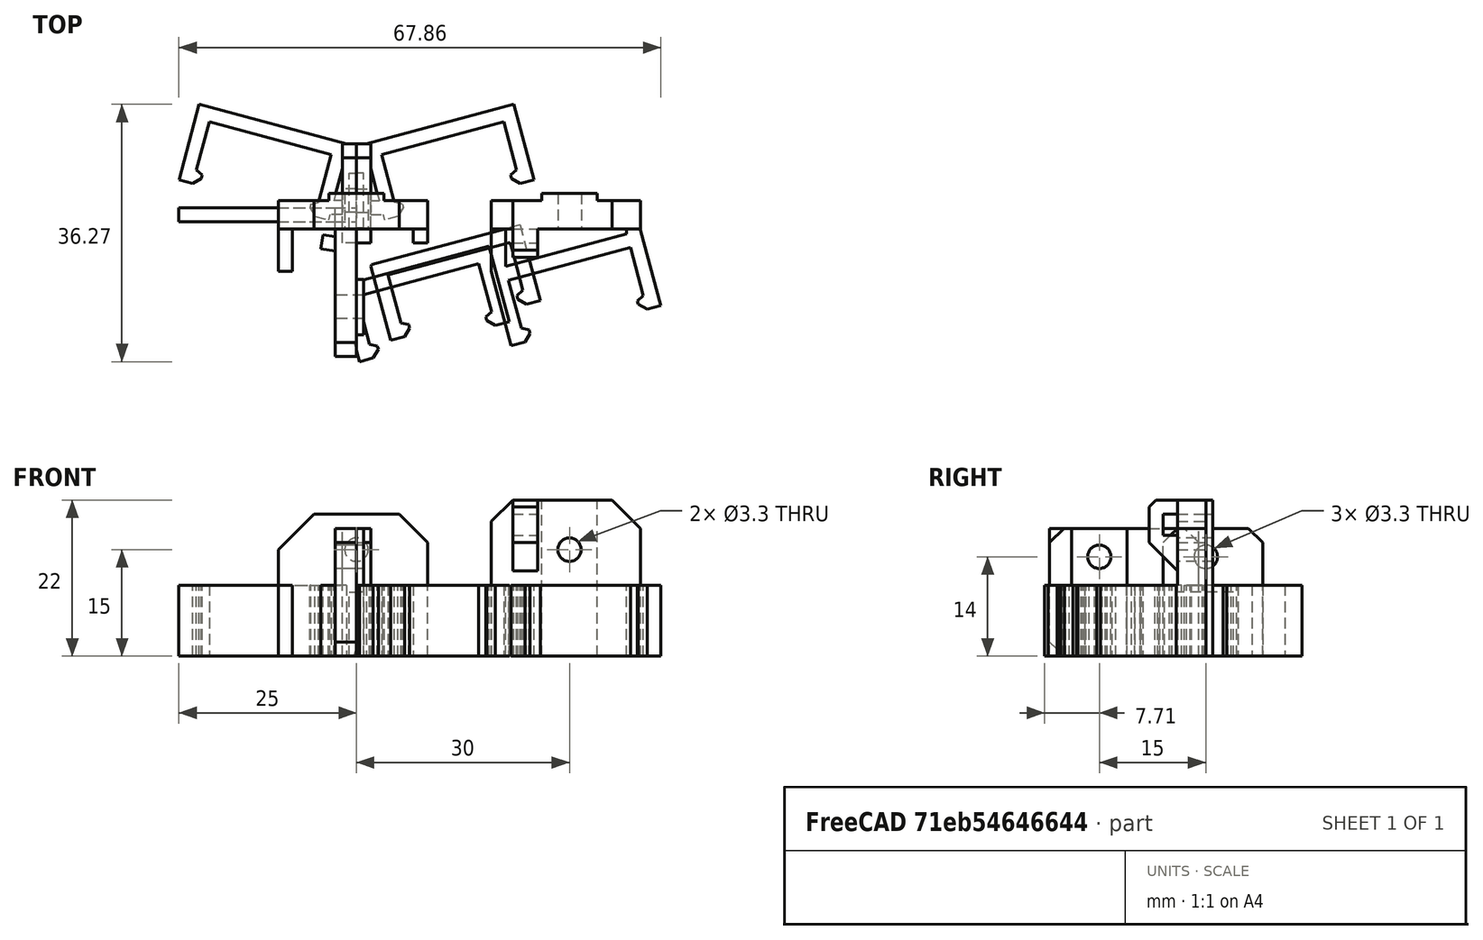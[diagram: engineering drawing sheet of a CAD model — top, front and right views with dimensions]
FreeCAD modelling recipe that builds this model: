
FCSTD DOCUMENT  (FreeCAD 0.19R24291 (Git))
Label: neopixel-mount
License: All rights reserved
LicenseURL: http://en.wikipedia.org/wiki/All_rights_reserved
objects: Part::Box×17, Part::Chamfer×9, Part::MultiFuse×8, Part::Cut×6, Part::Feature×5, Part::Cylinder×4, Part::Refine×3
note: 52 computed .brp shape members not serialized (recipe doc carries the construction recipe); baked Part::Feature solids carry a one-line shape summary decoded from their .brp

FEATURE [Part::Feature] Fusion038001001001001  label="arm"
  Placement = pos=(22.1478,-1.43999,0) rot=(0,0,1;3.40339rad)
  shape: bbox 23.9 x 16.27 x 10 mm, 16 faces (baked)
FEATURE [Part::Refine] Fusion038001001001001001  label="arm001"
  Placement = pos=(-2.5,-5,0) rot=(0,0,1;0rad)
  Source = -> Fusion038001001001001
FEATURE [Part::Box] Box001  label="Cube001"
  AttacherType = Attacher::AttachEngine3D
  Height = 10
  Length = 22
  Placement = pos=(-24,-3,0) rot=(0,0,1;0rad)
  Width = 2
FEATURE [Part::MultiFuse] Fusion  label="base-arm"
  Placement = pos=(-1,0,0) rot=(0,0,1;0rad)
  Shapes = -> [Fusion038001001001001001,Box001]
FEATURE [Part::Cylinder] Cylinder
  Angle = 360
  AttacherType = Attacher::AttachEngine3D
  Height = 6
  Placement = pos=(2,-15,14) rot=(0,-1,0;1.5708rad)
  Radius = 1.65
FEATURE [Part::Box] Box003  label="Cube003"
  AttacherType = Attacher::AttachEngine3D
  Height = 10
  Length = 3
  Placement = pos=(-5.03256,-6.77213,0) rot=(0,0,-1;0.174533rad)
  Width = 2
FEATURE [Part::MultiFuse] Fusion038001001001001002  label="base-arm-ext"
  Shapes = -> [Fusion,Box003]
FEATURE [Part::Box] Box004  label="Cube004"
  AttacherType = Attacher::AttachEngine3D
  Height = 18
  Length = 2
  Placement = pos=(-1,-18.9,0) rot=(0,0,1;0rad)
  Width = 7.8
FEATURE [Part::Box] Box002  label="Cube002"
  AttacherType = Attacher::AttachEngine3D
  Height = 18
  Length = 3
  Placement = pos=(-3,-22,0) rot=(0,0,1;0rad)
  Width = 21
FEATURE [Part::Box] Box005  label="Cube005"
  AttacherType = Attacher::AttachEngine3D
  Height = 18
  Length = 3
  Placement = pos=(-3,-22,0) rot=(0,0,1;0rad)
  Width = 21
FEATURE [Part::Chamfer] Chamfer
  Base = -> Box005
  Edges = 3 edges r=2: [Edge9,Edge10,Edge12]
FEATURE [Part::MultiFuse] Fusion038001001001001003
  Shapes = -> [Chamfer,Box004]
FEATURE [Part::Cut] Cut
  Base = -> Fusion038001001001001003
  Tool = -> Cylinder
FEATURE [Part::MultiFuse] Fusion038001001001001004
  Shapes = -> [Cut,Fusion038001001001001002]
FEATURE [Part::Box] Box  label="Cube"
  AttacherType = Attacher::AttachEngine3D
  Height = 20
  Length = 21
  Placement = pos=(-11,-4,0) rot=(0,0,1;0rad)
  Width = 4
FEATURE [Part::Refine] Fusion038001001001001005  label="arm002"
  Placement = pos=(0.9,-2,0) rot=(0,0,1;0rad)
  Source = -> Fusion038001001001001
FEATURE [Part::Box] Box006  label="Cube006"
  AttacherType = Attacher::AttachEngine3D
  Height = 10
  Length = 2
  Placement = pos=(-11,-10,0) rot=(0,0,1;0rad)
  Width = 9
FEATURE [Part::Box] Box007  label="Cube007"
  AttacherType = Attacher::AttachEngine3D
  Height = 10
  Length = 2
  Placement = pos=(8,-6,0) rot=(0,0,1;0rad)
  Width = 5
FEATURE [Part::Cylinder] Cylinder001
  Angle = 360
  AttacherType = Attacher::AttachEngine3D
  Height = 10
  Placement = pos=(0,4,15) rot=(1,0,0;1.5708rad)
  Radius = 1.65
FEATURE [Part::Box] Box008  label="Cube008"
  AttacherType = Attacher::AttachEngine3D
  Height = 20
  Length = 7.8
  Placement = pos=(-3.9,0,0) rot=(0,0,1;0rad)
  Width = 1
FEATURE [Part::Chamfer] Chamfer002
  Base = -> Fusion038001001001001005
  Edges = 1 edges r=0.17: [Edge39]
FEATURE [Part::MultiFuse] Fusion038001001001001006  label="side-arm-base"
  Shapes = -> [Box006,Chamfer002,Box007]
FEATURE [Part::Feature] Fusion038001001001001006001  label="side-arm-base001"
  Placement = pos=(30,0,0) rot=(0,0,1;0rad)
  shape: bbox 23.86 x 19.45 x 10 mm, 39 faces (baked)
FEATURE [Part::Box] Box010  label="Cube010"
  AttacherType = Attacher::AttachEngine3D
  Height = 22
  Length = 7.8
  Placement = pos=(26.1,0,0) rot=(0,0,1;0rad)
  Width = 1
FEATURE [Part::Box] Box011  label="Cube011"
  AttacherType = Attacher::AttachEngine3D
  Height = 22
  Length = 21
  Placement = pos=(19,-4,0) rot=(0,0,1;0rad)
  Width = 4
FEATURE [Part::Cylinder] Cylinder002
  Angle = 360
  AttacherType = Attacher::AttachEngine3D
  Height = 10
  Placement = pos=(30,4,15) rot=(1,0,0;1.5708rad)
  Radius = 1.65
FEATURE [Part::MultiFuse] Fusion038001001001001006002
  Shapes = -> [Box008,Box,Fusion038001001001001006]
FEATURE [Part::Chamfer] Chamfer003
  Base = -> Fusion038001001001001006002
  Edges = 1 edges r=5: [Edge9]
FEATURE [Part::Chamfer] Chamfer004
  Base = -> Chamfer003
  Edges = 1 edges r=4: [Edge29]
FEATURE [Part::Cut] Cut001
  Base = -> Chamfer004
  Tool = -> Cylinder001
FEATURE [Part::Box] Box012  label="Cube012"
  AttacherType = Attacher::AttachEngine3D
  Height = 10
  Length = 3.5
  Placement = pos=(22,-8,15) rot=(0,0,1;0rad)
  Width = 5
FEATURE [Part::Box] Box013  label="Cube013"
  AttacherType = Attacher::AttachEngine3D
  Height = 3
  Length = 6
  Placement = pos=(22,-6,20) rot=(0,0,1;0rad)
  Width = 2
FEATURE [Part::Chamfer] Chamfer007
  Base = -> Box011
  Edges = 1 edges r=3: [Edge2]
FEATURE [Part::Chamfer] Chamfer008
  Base = -> Chamfer007
  Edges = 1 edges r=4: [Edge15]
FEATURE [Part::Cut] Cut002
  Base = -> Box012
  Placement = pos=(0,0,-3) rot=(0,0,1;0rad)
  Tool = -> Box013
FEATURE [Part::Chamfer] Chamfer009
  Base = -> Cut002
  Edges = 1 edges r=4: [Edge9]
FEATURE [Part::Chamfer] Chamfer010
  Base = -> Chamfer009
  Edges = 1 edges r=1: [Edge12]
FEATURE [Part::MultiFuse] Fusion038001001001001006003
  Shapes = -> [Fusion038001001001001006001,Chamfer010,Chamfer008,Box010]
FEATURE [Part::Cut] Cut003
  Base = -> Fusion038001001001001006003
  Tool = -> Cylinder002
FEATURE [Part::Feature] Fusion038001001001001006004001  label="arm004"
  Placement = pos=(0,15,0) rot=(0,0,1;0rad)
  shape: bbox 23.9 x 16.27 x 10 mm, 16 faces (baked)
FEATURE [Part::Box] Box014  label="Cube014"
  AttacherType = Attacher::AttachEngine3D
  Height = 18
  Length = 2
  Placement = pos=(0,-6,0) rot=(0,0,1;0rad)
  Width = 14
FEATURE [Part::Box] Box015  label="Cube015"
  AttacherType = Attacher::AttachEngine3D
  Height = 18
  Length = 1
  Placement = pos=(-1,-3.9,0) rot=(0,0,1;0rad)
  Width = 7.8
FEATURE [Part::Box] Box016  label="Cube016"
  AttacherType = Attacher::AttachEngine3D
  Height = 10
  Length = 2
  Placement = pos=(2,-2,0) rot=(0,0,1;0rad)
  Width = 2
FEATURE [Part::Chamfer] Chamfer011
  Base = -> Box014
  Edges = 2 edges r=2: [Edge10,Edge12]
FEATURE [Part::MultiFuse] Fusion038001001001001006004002
  Shapes = -> [Chamfer011,Box016,Box015,Fusion038001001001001006004001]
FEATURE [Part::Cylinder] Cylinder003
  Angle = 360
  AttacherType = Attacher::AttachEngine3D
  Height = 10
  Placement = pos=(-2,0,14) rot=(0,1,0;1.5708rad)
  Radius = 1.65
FEATURE [Part::Cut] Cut004
  Base = -> Fusion038001001001001006004002
  Tool = -> Cylinder003
FEATURE [Part::Box] Box017  label="Cube017"
  AttacherType = Attacher::AttachEngine3D
  Height = 10
  Length = 10
  Placement = pos=(-10,-5,9) rot=(0,0,1;0rad)
  Width = 10
FEATURE [Part::Cut] Cut005
  Base = -> Cut004
  Tool = -> Box017
FEATURE [Part::Refine] Cut005001
  Source = -> Cut005
FEATURE [Part::Feature] Cut005001002  label="neo-pixel-arm"
  shape: bbox 25.99 x 19.56 x 18 mm, 31 faces (baked)
FEATURE [Part::Feature] Part__Mirroring001  label="neo-pixel-arm-rev"
  shape: bbox 25.99 x 19.56 x 18 mm, 31 faces (baked)
